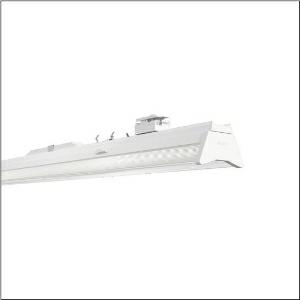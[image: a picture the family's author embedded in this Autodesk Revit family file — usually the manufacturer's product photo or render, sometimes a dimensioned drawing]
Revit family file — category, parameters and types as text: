
# Revit family: licross_11_performance_mo_51tm16dn4axg
name_source: partatom
category: Lighting Fixtures
units: mm (PartAtom-declared; Revit-internal decimal feet)

## family parameters
Cut with Voids When Loaded = No
Host = Face
Light Source = No
Part Type = Normal
Room Calculation Point = No
Round Connector Dimension = Use Diameter
Shared = No

## types (1)
- --- (1 x LED, 10110 lm, 57.1 W, 4000K)
    Apparent Load = 57 VA
    CIE Flux Codes = 66 88 96 79 100
    Color Rendering = 80
    Color Temperature = 4000K
    Default Elevation = 1800 mm
    Description = Licross 11 Performance MO, luminaire insert, of sheet steel, galvanised, coil coated, white, length: 1.500mm, width: 120mm, height: 123mm, LED rated luminous flux: 10.110lm, light colour: 840, SDCM (Standard Deviation of Colour Matching)MacAdam ≤ 2 SDCM (initial), control gear: DALI 2, with plug, 5-pole, with phase selection, mains connection: 220..240V, AC, 50/60Hz, rated input power: 57W, internal wiring halogen-free, primary light control with lens, of plastic, primary optical cover: cover, of PMMA, light emission: direct/indirect distribution, primary light characteristic: symmetric, protection rating (complete): IP40, insulation class (complete): insulation class I (protective earthing), certification: CE, ENEC, VDE, UKCA, protection symbol: D if used in an environment without relevant dust loads with corresponding accessories, impact resistance: IK06, permissible ambient temperature for indoor applications: -25..+35°C, corresponds to IFS (International Featured Standards) requirements for safety and quality in the food industry, reducing of maximum allowable ambient temperature of 5°C with ceiling mounting, LABS conformity tested according to VDMA 24364:2018-05, The light source and the operating device comply with the requirements of the Ecodesign Regulation (EU) 2019/2020 and are replaceable in accordance with this regulation, packaging unit: 1 piece
    Height = 114 mm
    Lamp = 1 x LED
    Lamp Light Flux = 10110 lm
    Lamp Power = 57.1 W
    Lamp count = 1
    Length = 1500 mm
    Luminous efficacy = 177 lm/W
    Manufacturer = Siteco
    ModVariant = No
    Model = 51TM16DN4AXG
    Mounting Place = Ceiling
    Mounting Type = Pendant
    Number of Poles = 1
    OnlyDefault = Yes
    Power Factor = 1
    Product Name = Licross 11 Performance MO
    Product group = luminaire insert | ceiling pendant
    ProductGroupID = 901
    Protection Class = Protection class I
    Protection Degree = IP 40
    RLX_Detail_Level = 1
    RLX_Emergency_Light_Flux = 0 lm
    RLX_Emergency_Type = 0
    RLX_Emergency_Type_DB = No
    RlxData = <blob elided: 34285 chars, md5=d1085780>
    Socket = socket
    Standby Power = 0 W
    System Light Flux = 10110 lm
    System Power = 57 W
    Type Comments = factory setting: luminous flux: 100 % | dim-lin: 254 | 378 mA
    Type Image = l_1256138.jpg
    URL = http://relux.com
    VarID = @adj_102893
    Voltage = 0 V
    Weight = 0.00 kg
    Width = 120 mm

## geometry (parser evidence)
native form markers: Blend x4, Sweep x10
no freeform markers — native parametric forms only
